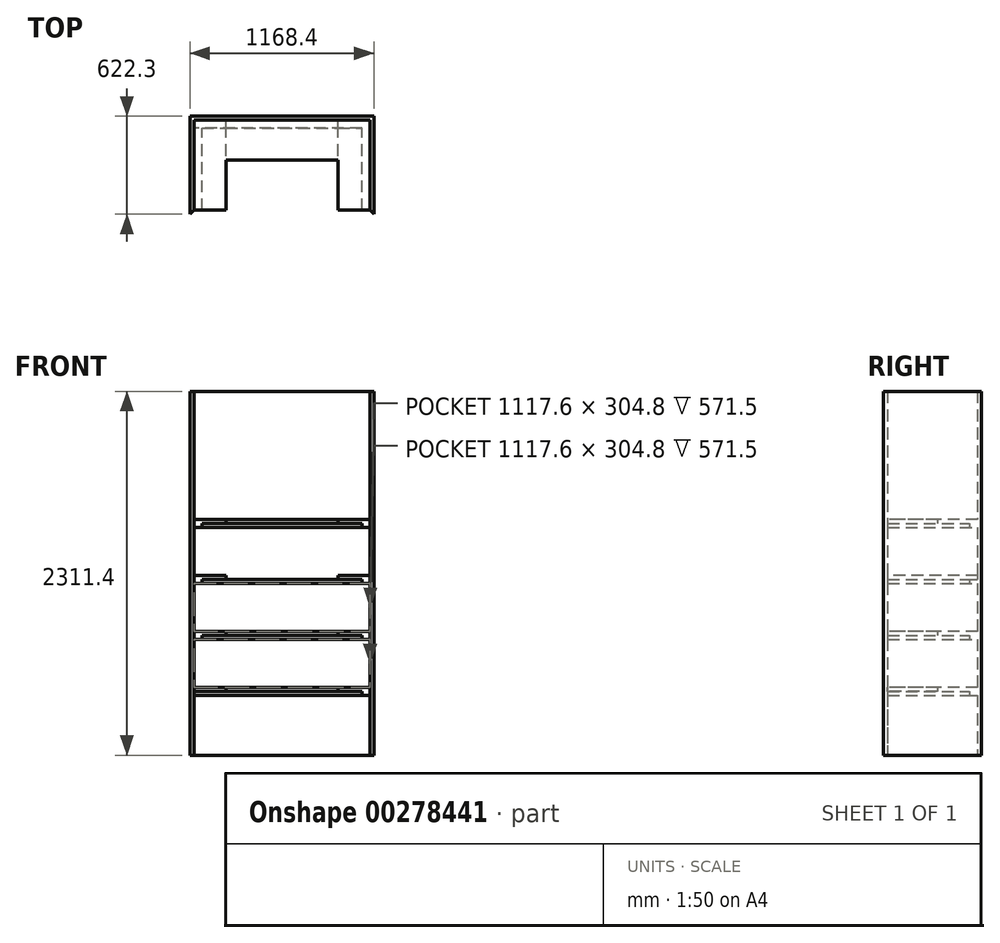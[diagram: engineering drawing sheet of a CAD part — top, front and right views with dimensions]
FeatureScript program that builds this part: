
annotation { "Feature Type Name" : "Feature", "Feature Type Description" : "" }
export const myFeature = defineFeature(function(context is Context, id is Id, definition is map)
    precondition{}
    {
        {
            var Q0;
            Q0=qCreatedBy(makeId("Top.planeOp"),FACE);
            var sketch = newSketch(context, id + "F0", { "sketchPlane" : qUnion([Q0])});
            skLineSegment(sketch, "E0.bottom", {"start": v(558.8, -285.75) * mm, "end": v(368.3, -285.75) * mm});
            skLineSegment(sketch, "E0.top", {"start": v(558.8, 285.75) * mm, "end": v(-558.8, 285.75) * mm});
            skLineSegment(sketch, "E0.left", {"start": v(558.8, -285.75) * mm, "end": v(558.8, 285.75) * mm});
            skLineSegment(sketch, "E0.right", {"start": v(-558.8, -285.75) * mm, "end": v(-558.8, 285.75) * mm});
            skPoint(sketch, "E0.middle", {"position": v(0, 0) * mm});
            skPoint(sketch, "E1", {"position": v(368.3, -285.75) * mm});
            skPoint(sketch, "E2", {"position": v(-368.3, -285.75) * mm});
            skLineSegment(sketch, "E3", {"start": v(-368.3, -285.75) * mm, "end": v(-558.8, -285.75) * mm});
            skLineSegment(sketch, "E4.0", {"start": v(584.2, -311.15) * mm, "end": v(368.3, -311.15) * mm});
            skLineSegment(sketch, "E4.1", {"start": v(-368.3, -311.15) * mm, "end": v(-584.2, -311.15) * mm});
            skLineSegment(sketch, "E4.2", {"start": v(-584.2, -311.15) * mm, "end": v(-584.2, 311.15) * mm});
            skLineSegment(sketch, "E4.3", {"start": v(584.2, 311.15) * mm, "end": v(-584.2, 311.15) * mm});
            skLineSegment(sketch, "E4.4", {"start": v(584.2, -311.15) * mm, "end": v(584.2, 311.15) * mm});
            skLineSegment(sketch, "E5", {"start": v(-368.3, -285.75) * mm, "end": v(-368.3, -311.15) * mm});
            skLineSegment(sketch, "E6", {"start": v(368.3, -285.75) * mm, "end": v(368.3, -311.15) * mm});
            skLineSegment(sketch, "E7", {"start": v(-558.8, -285.75) * mm, "end": v(-584.2, -311.15) * mm});
            skLineSegment(sketch, "E8", {"start": v(558.8, -285.75) * mm, "end": v(584.2, -311.15) * mm});
            skLineSegment(sketch, "E9", {"start": v(-584.2, 311.15) * mm, "end": v(-558.8, 285.75) * mm});
            skLineSegment(sketch, "E10", {"start": v(584.2, 311.15) * mm, "end": v(558.8, 285.75) * mm});
            skSolve(sketch);
        }
        {
            var Q0;
            Q0=makeQuery(id+"F0.imprint","IMPRINT",FACE,{"disambiguationData":[TD([[makeQuery(id+"F0.imprint","IMPRINT",EDGE,{"derivedFrom":sQuery(id+"F0.wireOp",EDGE,"E0.top")}),-1.0]])]});
            extrude(context, id + "F1", {"entities" : qUnion([Q0]), "depth" : 2311.4 * mm});
        }
        {
            var Q0;
            Q0=makeQuery(id+"F1.opExtrude","SWEPT_FACE",FACE,{"disambiguationData":[OSD([sQuery(id+"F0.wireOp",EDGE,"E0.top")])]});
            var sketch = newSketch(context, id + "F2", { "sketchPlane" : qUnion([Q0])});
            skLineSegment(sketch, "E11.0", {"start": v(-558.8, 2311.4) * mm, "end": v(-558.8, 0) * mm});
            skLineSegment(sketch, "E12.0", {"start": v(558.8, 0) * mm, "end": v(-558.8, 0) * mm});
            skLineSegment(sketch, "E13.0", {"start": v(558.8, 2311.4) * mm, "end": v(-558.8, 2311.4) * mm});
            skLineSegment(sketch, "E14.0", {"start": v(558.8, 2311.4) * mm, "end": v(558.8, 0) * mm});
            skLineSegment(sketch, "E15", {"start": v(-558.8, 406.4) * mm, "end": v(558.8, 406.4) * mm});
            skLineSegment(sketch, "E16", {"start": v(558.8, 381) * mm, "end": v(-558.8, 381) * mm});
            skLineSegment(sketch, "E17", {"start": v(-558.8, 736.6) * mm, "end": v(558.8, 736.6) * mm});
            skLineSegment(sketch, "E18", {"start": v(-558.8, 762) * mm, "end": v(558.8, 762) * mm});
            skLineSegment(sketch, "E19", {"start": v(-558.8, 1092.2) * mm, "end": v(558.8, 1092.2) * mm});
            skLineSegment(sketch, "E20", {"start": v(-558.8, 1117.6) * mm, "end": v(558.8, 1117.6) * mm});
            skLineSegment(sketch, "E21.top", {"start": v(-558.8, 431.8) * mm, "end": v(558.8, 431.8) * mm});
            skLineSegment(sketch, "E21.left", {"start": v(-558.8, 406.4) * mm, "end": v(-558.8, 431.8) * mm});
            skLineSegment(sketch, "E21.right", {"start": v(558.8, 406.4) * mm, "end": v(558.8, 431.8) * mm});
            skLineSegment(sketch, "E22.top", {"start": v(-558.8, 787.4) * mm, "end": v(558.8, 787.4) * mm});
            skLineSegment(sketch, "E22.left", {"start": v(-558.8, 762) * mm, "end": v(-558.8, 787.4) * mm});
            skLineSegment(sketch, "E22.right", {"start": v(558.8, 762) * mm, "end": v(558.8, 787.4) * mm});
            skLineSegment(sketch, "E23.top", {"start": v(-558.8, 1143) * mm, "end": v(558.8, 1143) * mm});
            skLineSegment(sketch, "E23.left", {"start": v(-558.8, 1117.6) * mm, "end": v(-558.8, 1143) * mm});
            skLineSegment(sketch, "E23.right", {"start": v(558.8, 1117.6) * mm, "end": v(558.8, 1143) * mm});
            skLineSegment(sketch, "E24.bottom", {"start": v(558.8, 1447.8) * mm, "end": v(-558.8, 1447.8) * mm});
            skLineSegment(sketch, "E24.top", {"start": v(558.8, 1473.2) * mm, "end": v(-558.8, 1473.2) * mm});
            skLineSegment(sketch, "E24.left", {"start": v(558.8, 1447.8) * mm, "end": v(558.8, 1473.2) * mm});
            skLineSegment(sketch, "E24.right", {"start": v(-558.8, 1447.8) * mm, "end": v(-558.8, 1473.2) * mm});
            skLineSegment(sketch, "E25", {"start": v(558.8, 1498.6) * mm, "end": v(-558.8, 1498.6) * mm});
            skSolve(sketch);
        }
        {
            var Q0;
            Q0=makeQuery(id+"F0.imprint","IMPRINT",FACE,{"disambiguationData":[TD([[makeQuery(id+"F0.imprint","IMPRINT",EDGE,{"derivedFrom":sQuery(id+"F0.wireOp",EDGE,"E0.right")}),1.0]])]});
            extrude(context, id + "F3", {"entities" : qUnion([Q0]), "operationType" : NewBodyOperationType.ADD, "depth" : 2311.4 * mm});
        }
        {
            var Q0;
            Q0=makeQuery(id+"F0.imprint","IMPRINT",FACE,{"disambiguationData":[TD([[makeQuery(id+"F0.imprint","IMPRINT",EDGE,{"derivedFrom":sQuery(id+"F0.wireOp",EDGE,"E0.left")}),-1.0]])]});
            extrude(context, id + "F4", {"entities" : qUnion([Q0]), "operationType" : NewBodyOperationType.ADD, "depth" : 2311.4 * mm});
        }
        {
            var Q0;
            Q0=makeQuery(id+"F3.opExtrude","SWEPT_FACE",FACE,{"disambiguationData":[OSD([sQuery(id+"F0.wireOp",EDGE,"E4.2")])]});
            var sketch = newSketch(context, id + "F5", { "sketchPlane" : qUnion([Q0])});
            skLineSegment(sketch, "E26.0", {"start": v(311.15, 2311.4) * mm, "end": v(311.15, 0) * mm});
            skLineSegment(sketch, "E27.0", {"start": v(-285.75, 2311.4) * mm, "end": v(-285.75, 0) * mm});
            skLineSegment(sketch, "E28.0", {"start": v(311.15, 0) * mm, "end": v(-311.15, 0) * mm});
            skPoint(sketch, "E29", {"position": v(311.15, 381) * mm});
            skPoint(sketch, "E30", {"position": v(311.15, 406.4) * mm});
            skPoint(sketch, "E31", {"position": v(311.15, 431.8) * mm});
            skPoint(sketch, "E32", {"position": v(311.15, 736.6) * mm});
            skPoint(sketch, "E33", {"position": v(311.15, 762) * mm});
            skPoint(sketch, "E34", {"position": v(311.15, 787.4) * mm});
            skPoint(sketch, "E35", {"position": v(311.15, 1092.2) * mm});
            skPoint(sketch, "E36", {"position": v(311.15, 1117.6) * mm});
            skPoint(sketch, "E37", {"position": v(311.15, 1143) * mm});
            skPoint(sketch, "E38", {"position": v(311.15, 0) * mm});
            skPoint(sketch, "E39", {"position": v(311.15, 2057.4) * mm});
            skLineSegment(sketch, "E40.left", {"start": v(311.15, 736.6) * mm, "end": v(311.15, 762) * mm});
            skLineSegment(sketch, "E40.right", {"start": v(-285.75, 736.6) * mm, "end": v(-285.75, 762) * mm});
            skLineSegment(sketch, "E41.left", {"start": v(311.15, 1092.2) * mm, "end": v(311.15, 1117.6) * mm});
            skLineSegment(sketch, "E41.right", {"start": v(-285.75, 1092.2) * mm, "end": v(-285.75, 1117.6) * mm});
            skPoint(sketch, "E42", {"position": v(311.15, 1447.8) * mm});
            skPoint(sketch, "E43", {"position": v(311.15, 1473.2) * mm});
            skPoint(sketch, "E44", {"position": v(311.15, 1498.6) * mm});
            skLineSegment(sketch, "E45.left", {"start": v(311.15, 1473.2) * mm, "end": v(311.15, 1498.6) * mm});
            skLineSegment(sketch, "E45.right", {"start": v(-285.75, 1473.2) * mm, "end": v(-285.75, 1498.6) * mm});
            skLineSegment(sketch, "E46.0", {"start": v(285.75, 2311.4) * mm, "end": v(285.75, 0) * mm});
            skPoint(sketch, "E47", {"position": v(285.75, 1498.6) * mm});
            skPoint(sketch, "E48", {"position": v(285.75, 1473.2) * mm});
            skPoint(sketch, "E49", {"position": v(285.75, 1447.8) * mm});
            skLineSegment(sketch, "E50", {"start": v(285.75, 1498.6) * mm, "end": v(-285.75, 1498.6) * mm});
            skLineSegment(sketch, "E51", {"start": v(285.75, 1473.2) * mm, "end": v(-285.75, 1473.2) * mm});
            skLineSegment(sketch, "E52", {"start": v(285.75, 1447.8) * mm, "end": v(-285.75, 1447.8) * mm});
            skLineSegment(sketch, "E53", {"start": v(285.75, 1092.2) * mm, "end": v(-285.75, 1092.2) * mm});
            skLineSegment(sketch, "E54", {"start": v(285.75, 1117.6) * mm, "end": v(-285.75, 1117.6) * mm});
            skLineSegment(sketch, "E55", {"start": v(285.75, 1143) * mm, "end": v(-285.75, 1143) * mm});
            skLineSegment(sketch, "E56", {"start": v(285.75, 787.4) * mm, "end": v(-285.75, 787.4) * mm});
            skLineSegment(sketch, "E57", {"start": v(285.75, 762) * mm, "end": v(-285.75, 762) * mm});
            skLineSegment(sketch, "E58", {"start": v(285.75, 736.6) * mm, "end": v(-285.75, 736.6) * mm});
            skLineSegment(sketch, "E59", {"start": v(285.75, 381) * mm, "end": v(-285.75, 381) * mm});
            skLineSegment(sketch, "E60", {"start": v(285.75, 406.4) * mm, "end": v(-285.75, 406.4) * mm});
            skLineSegment(sketch, "E61", {"start": v(285.75, 431.8) * mm, "end": v(-285.75, 431.8) * mm});
            skSolve(sketch);
        }
        {
            var Q0;
            Q0=makeQuery(id+"F3.opExtrude","SWEPT_FACE",FACE,{"disambiguationData":[OSD([sQuery(id+"F0.wireOp",EDGE,"E4.2")])]});
            var sketch = newSketch(context, id + "F6", { "sketchPlane" : qUnion([Q0])});
            skLineSegment(sketch, "E62.0", {"start": v(311.15, 2311.4) * mm, "end": v(311.15, 0) * mm});
            skLineSegment(sketch, "E63.0", {"start": v(311.15, 0) * mm, "end": v(-311.15, 0) * mm});
            skLineSegment(sketch, "E64.0", {"start": v(-285.75, 2311.4) * mm, "end": v(-285.75, 0) * mm});
            skPoint(sketch, "E65", {"position": v(311.15, 381) * mm});
            skPoint(sketch, "E66", {"position": v(-285.75, 381) * mm});
            skPoint(sketch, "E67", {"position": v(311.15, 406.4) * mm});
            skPoint(sketch, "E68", {"position": v(311.15, 431.8) * mm});
            skLineSegment(sketch, "E69", {"start": v(311.15, 381) * mm, "end": v(-285.75, 381) * mm});
            skLineSegment(sketch, "E70", {"start": v(311.15, 406.4) * mm, "end": v(-285.75, 406.4) * mm});
            skLineSegment(sketch, "E71", {"start": v(311.15, 431.8) * mm, "end": v(-285.75, 431.8) * mm});
            skSolve(sketch);
        }
        {
            var Q0;
            Q0=makeQuery(id+"F3.opExtrude","SWEPT_FACE",FACE,{"disambiguationData":[OSD([sQuery(id+"F0.wireOp",EDGE,"E0.right")])]});
            var sketch = newSketch(context, id + "F7", { "sketchPlane" : qUnion([Q0])});
            skLineSegment(sketch, "E72.0", {"start": v(-285.75, 2311.4) * mm, "end": v(-285.75, 0) * mm});
            skLineSegment(sketch, "E73.0", {"start": v(285.75, 2311.4) * mm, "end": v(285.75, 0) * mm});
            skLineSegment(sketch, "E74.0", {"start": v(-311.15, 381) * mm, "end": v(285.75, 381) * mm});
            skLineSegment(sketch, "E75.0", {"start": v(-311.15, 406.4) * mm, "end": v(285.75, 406.4) * mm});
            skLineSegment(sketch, "E76.0", {"start": v(-311.15, 431.8) * mm, "end": v(285.75, 431.8) * mm});
            skLineSegment(sketch, "E77.0", {"start": v(-285.75, 736.6) * mm, "end": v(285.75, 736.6) * mm});
            skLineSegment(sketch, "E78.0", {"start": v(-285.75, 762) * mm, "end": v(285.75, 762) * mm});
            skLineSegment(sketch, "E79.0", {"start": v(-285.75, 787.4) * mm, "end": v(285.75, 787.4) * mm});
            skLineSegment(sketch, "E80.0", {"start": v(-285.75, 1092.2) * mm, "end": v(285.75, 1092.2) * mm});
            skLineSegment(sketch, "E81.0", {"start": v(-285.75, 1117.6) * mm, "end": v(285.75, 1117.6) * mm});
            skLineSegment(sketch, "E82.0", {"start": v(-285.75, 1143) * mm, "end": v(285.75, 1143) * mm});
            skLineSegment(sketch, "E83.0", {"start": v(-285.75, 1447.8) * mm, "end": v(285.75, 1447.8) * mm});
            skLineSegment(sketch, "E84.0", {"start": v(-285.75, 1473.2) * mm, "end": v(285.75, 1473.2) * mm});
            skLineSegment(sketch, "E85.0", {"start": v(-285.75, 1498.6) * mm, "end": v(285.75, 1498.6) * mm});
            skLineSegment(sketch, "E86.0", {"start": v(-285.75, 2311.4) * mm, "end": v(285.75, 2311.4) * mm});
            skLineSegment(sketch, "E87", {"start": v(-285.75, 431.8) * mm, "end": v(285.75, 431.8) * mm});
            skLineSegment(sketch, "E88", {"start": v(-285.75, 406.4) * mm, "end": v(285.75, 406.4) * mm});
            skLineSegment(sketch, "E89", {"start": v(-285.75, 381) * mm, "end": v(285.75, 381) * mm});
            skSolve(sketch);
        }
        {
            var Q0;
            Q0=makeQuery(id+"F4.opExtrude","SWEPT_FACE",FACE,{"disambiguationData":[OSD([sQuery(id+"F0.wireOp",EDGE,"E0.left")])]});
            var sketch = newSketch(context, id + "F8", { "sketchPlane" : qUnion([Q0])});
            skLineSegment(sketch, "E90.0.0", {"start": v(311.15, 0) * mm, "end": v(311.15, 381) * mm});
            skLineSegment(sketch, "E90.0.1", {"start": v(311.15, 381) * mm, "end": v(-285.75, 381) * mm});
            skLineSegment(sketch, "E90.0.2", {"start": v(-285.75, 381) * mm, "end": v(-285.75, 0) * mm});
            skLineSegment(sketch, "E90.0.3", {"start": v(-285.75, 0) * mm, "end": v(311.15, 0) * mm});
            skLineSegment(sketch, "E91.0", {"start": v(285.75, 2311.4) * mm, "end": v(285.75, 0) * mm});
            skLineSegment(sketch, "E92.0.0", {"start": v(311.15, 381) * mm, "end": v(311.15, 406.4) * mm});
            skLineSegment(sketch, "E92.0.1", {"start": v(311.15, 406.4) * mm, "end": v(-285.75, 406.4) * mm});
            skLineSegment(sketch, "E92.0.2", {"start": v(-285.75, 406.4) * mm, "end": v(-285.75, 381) * mm});
            skLineSegment(sketch, "E92.0.3", {"start": v(-285.75, 381) * mm, "end": v(311.15, 381) * mm});
            skLineSegment(sketch, "E93.0.0", {"start": v(311.15, 406.4) * mm, "end": v(311.15, 431.8) * mm});
            skLineSegment(sketch, "E93.0.1", {"start": v(311.15, 431.8) * mm, "end": v(-285.75, 431.8) * mm});
            skLineSegment(sketch, "E93.0.2", {"start": v(-285.75, 431.8) * mm, "end": v(-285.75, 406.4) * mm});
            skLineSegment(sketch, "E93.0.3", {"start": v(-285.75, 406.4) * mm, "end": v(311.15, 406.4) * mm});
            skLineSegment(sketch, "E94.0.0", {"start": v(-285.75, 431.8) * mm, "end": v(311.15, 431.8) * mm});
            skLineSegment(sketch, "E94.0.1", {"start": v(311.15, 431.8) * mm, "end": v(311.15, 2311.4) * mm});
            skLineSegment(sketch, "E94.0.2", {"start": v(311.15, 2311.4) * mm, "end": v(-285.75, 2311.4) * mm});
            skLineSegment(sketch, "E94.0.3", {"start": v(-285.75, 2311.4) * mm, "end": v(-285.75, 431.8) * mm});
            skLineSegment(sketch, "E95.0", {"start": v(285.75, 736.6) * mm, "end": v(-285.75, 736.6) * mm});
            skLineSegment(sketch, "E96.0", {"start": v(285.75, 762) * mm, "end": v(-285.75, 762) * mm});
            skLineSegment(sketch, "E97.0", {"start": v(285.75, 787.4) * mm, "end": v(-285.75, 787.4) * mm});
            skLineSegment(sketch, "E98.0", {"start": v(285.75, 1092.2) * mm, "end": v(-285.75, 1092.2) * mm});
            skLineSegment(sketch, "E99.0", {"start": v(285.75, 1473.2) * mm, "end": v(-285.75, 1473.2) * mm});
            skLineSegment(sketch, "E100.0", {"start": v(285.75, 1447.8) * mm, "end": v(-285.75, 1447.8) * mm});
            skLineSegment(sketch, "E101.0", {"start": v(285.75, 1498.6) * mm, "end": v(-285.75, 1498.6) * mm});
            skLineSegment(sketch, "E102.0.0", {"start": v(285.75, 1498.6) * mm, "end": v(285.75, 2311.4) * mm});
            skLineSegment(sketch, "E102.0.1", {"start": v(285.75, 2311.4) * mm, "end": v(-285.75, 2311.4) * mm});
            skLineSegment(sketch, "E102.0.2", {"start": v(-285.75, 2311.4) * mm, "end": v(-285.75, 1498.6) * mm});
            skLineSegment(sketch, "E102.0.3", {"start": v(-285.75, 1498.6) * mm, "end": v(285.75, 1498.6) * mm});
            skLineSegment(sketch, "E103.0", {"start": v(285.75, 1117.6) * mm, "end": v(-285.75, 1117.6) * mm});
            skLineSegment(sketch, "E104.0", {"start": v(285.75, 1143) * mm, "end": v(-285.75, 1143) * mm});
            skSolve(sketch);
        }
        {
            var Q0;
            {var subQ0=sQuery(id+"F2.wireOp",EDGE,"E16");Q0=makeQuery(id+"F2.imprint","IMPRINT",FACE,{"disambiguationData":[TD([[makeQuery(id+"F2.imprint","IMPRINT",EDGE,{"derivedFrom":subQ0}),-1.0]])]});}
            var Q1;
            {var subQ0=sQuery(id+"F2.wireOp",EDGE,"E17");Q1=makeQuery(id+"F2.imprint","IMPRINT",FACE,{"disambiguationData":[TD([[makeQuery(id+"F2.imprint","IMPRINT",EDGE,{"derivedFrom":subQ0}),1.0]])]});}
            var Q2;
            {var subQ0=sQuery(id+"F2.wireOp",EDGE,"E19");Q2=makeQuery(id+"F2.imprint","IMPRINT",FACE,{"disambiguationData":[TD([[makeQuery(id+"F2.imprint","IMPRINT",EDGE,{"derivedFrom":subQ0}),1.0]])]});}
            var Q3;
            Q3=makeQuery(id+"F2.imprint","IMPRINT",FACE,{"disambiguationData":[TD([[makeQuery(id+"F2.imprint","IMPRINT",EDGE,{"derivedFrom":sQuery(id+"F2.wireOp",EDGE,"E24.bottom")}),-1.0]])]});
            extrude(context, id + "F9", {"entities" : qUnion([Q0, Q1, Q2, Q3]), "operationType" : NewBodyOperationType.ADD, "depth" : 50.8 * mm});
        }
        {
            var Q0;
            {var subQ0=sQuery(id+"F7.wireOp",EDGE,"E83.0");Q0=makeQuery(id+"F7.imprint","IMPRINT",FACE,{"disambiguationData":[TD([[makeQuery(id+"F7.imprint","IMPRINT",EDGE,{"derivedFrom":subQ0}),1.0]])]});}
            var Q1;
            {var subQ0=sQuery(id+"F7.wireOp",EDGE,"E80.0");Q1=makeQuery(id+"F7.imprint","IMPRINT",FACE,{"disambiguationData":[TD([[makeQuery(id+"F7.imprint","IMPRINT",EDGE,{"derivedFrom":subQ0}),1.0]])]});}
            var Q2;
            {var subQ0=sQuery(id+"F7.wireOp",EDGE,"E77.0");Q2=makeQuery(id+"F7.imprint","IMPRINT",FACE,{"disambiguationData":[TD([[makeQuery(id+"F7.imprint","IMPRINT",EDGE,{"derivedFrom":subQ0}),1.0]])]});}
            var Q3;
            {var subQ2=sQuery(id+"F7.wireOp",EDGE,"E88");Q3=makeQuery(id+"F7.imprint","IMPRINT",FACE,{"disambiguationData":[TD([[makeQuery(id+"F7.imprint","IMPRINT",EDGE,{"derivedFrom":subQ2}),-1.0]])]});}
            extrude(context, id + "F10", {"entities" : qUnion([Q0, Q1, Q2, Q3]), "operationType" : NewBodyOperationType.ADD, "depth" : 50.8 * mm});
        }
        {
            var Q0;
            {var subQ5=sQuery(id+"F8.wireOp",EDGE,"E92.0.2");Q0=makeQuery(id+"F8.imprint","IMPRINT",FACE,{"disambiguationData":[TD([[makeQuery(id+"F8.imprint","IMPRINT",EDGE,{"derivedFrom":subQ5}),1.0]])]});}
            var Q1;
            {var subQ0=sQuery(id+"F8.wireOp",EDGE,"E95.0");Q1=makeQuery(id+"F8.imprint","IMPRINT",FACE,{"disambiguationData":[TD([[makeQuery(id+"F8.imprint","IMPRINT",EDGE,{"derivedFrom":subQ0}),-1.0]])]});}
            var Q2;
            {var subQ0=sQuery(id+"F8.wireOp",EDGE,"E98.0");Q2=makeQuery(id+"F8.imprint","IMPRINT",FACE,{"disambiguationData":[TD([[makeQuery(id+"F8.imprint","IMPRINT",EDGE,{"derivedFrom":subQ0}),-1.0]])]});}
            var Q3;
            {var subQ0=sQuery(id+"F8.wireOp",EDGE,"E100.0");Q3=makeQuery(id+"F8.imprint","IMPRINT",FACE,{"disambiguationData":[TD([[makeQuery(id+"F8.imprint","IMPRINT",EDGE,{"derivedFrom":subQ0}),-1.0]])]});}
            extrude(context, id + "F11", {"entities" : qUnion([Q0, Q1, Q2, Q3]), "operationType" : NewBodyOperationType.ADD, "depth" : 50.8 * mm});
        }
        {
            var Q0;
            Q0=makeQuery(id+"F10.boolean.opBoolean","SPLIT",FACE,{"disambiguationData":[TD([makeQuery(id+"F9.opExtrude","SWEPT_FACE",FACE,{"disambiguationData":[OSD([sQuery(id+"F2.wireOp",EDGE,"E20")])]})])],"derivedFrom":makeQuery(id+"F3.opExtrude","SWEPT_FACE",FACE,{"disambiguationData":[OSD([sQuery(id+"F0.wireOp",EDGE,"E0.right")])]})});
            var sketch = newSketch(context, id + "F12", { "sketchPlane" : qUnion([Q0])});
            skLineSegment(sketch, "E105.0", {"start": v(-285.75, 431.8) * mm, "end": v(285.75, 431.8) * mm});
            skLineSegment(sketch, "E106.0", {"start": v(-285.75, 787.4) * mm, "end": v(285.75, 787.4) * mm});
            skLineSegment(sketch, "E107.0", {"start": v(-285.75, 1143) * mm, "end": v(285.75, 1143) * mm});
            skLineSegment(sketch, "E108.0", {"start": v(-285.75, 1498.6) * mm, "end": v(285.75, 1498.6) * mm});
            skLineSegment(sketch, "E109.0", {"start": v(-285.75, 736.6) * mm, "end": v(-285.75, 406.4) * mm});
            skLineSegment(sketch, "E110.0", {"start": v(285.75, 2311.4) * mm, "end": v(285.75, 0) * mm});
            skLineSegment(sketch, "E111.0", {"start": v(-285.75, 406.4) * mm, "end": v(285.75, 406.4) * mm});
            skLineSegment(sketch, "E112.0.0", {"start": v(-311.15, 0) * mm, "end": v(-285.75, 0) * mm});
            skLineSegment(sketch, "E112.0.1", {"start": v(-285.75, 0) * mm, "end": v(-285.75, 381) * mm});
            skLineSegment(sketch, "E112.0.2", {"start": v(-285.75, 381) * mm, "end": v(-285.75, 406.4) * mm});
            skLineSegment(sketch, "E112.0.3", {"start": v(-285.75, 406.4) * mm, "end": v(-285.75, 736.6) * mm});
            skLineSegment(sketch, "E112.0.4", {"start": v(-285.75, 736.6) * mm, "end": v(-285.75, 762) * mm});
            skLineSegment(sketch, "E112.0.5", {"start": v(-285.75, 762) * mm, "end": v(-285.75, 1092.2) * mm});
            skLineSegment(sketch, "E112.0.6", {"start": v(-285.75, 1092.2) * mm, "end": v(-285.75, 1117.6) * mm});
            skLineSegment(sketch, "E112.0.7", {"start": v(-285.75, 1117.6) * mm, "end": v(-285.75, 1447.8) * mm});
            skLineSegment(sketch, "E112.0.8", {"start": v(-285.75, 1447.8) * mm, "end": v(-285.75, 1473.2) * mm});
            skLineSegment(sketch, "E112.0.9", {"start": v(-285.75, 1473.2) * mm, "end": v(-285.75, 2311.4) * mm});
            skLineSegment(sketch, "E112.0.10", {"start": v(-285.75, 2311.4) * mm, "end": v(-311.15, 2311.4) * mm});
            skLineSegment(sketch, "E112.0.11", {"start": v(-311.15, 2311.4) * mm, "end": v(-311.15, 0) * mm});
            skLineSegment(sketch, "E113.0", {"start": v(-285.75, 762) * mm, "end": v(285.75, 762) * mm});
            skLineSegment(sketch, "E114.0.0", {"start": v(-285.75, 1117.6) * mm, "end": v(285.75, 1117.6) * mm});
            skLineSegment(sketch, "E114.0.2", {"start": v(285.75, 1117.6) * mm, "end": v(-285.75, 1117.6) * mm});
            skLineSegment(sketch, "E114.0.4", {"start": v(-285.75, 1117.6) * mm, "end": v(234.95, 1117.6) * mm});
            skLineSegment(sketch, "E114.0.6", {"start": v(234.95, 1117.6) * mm, "end": v(-285.75, 1117.6) * mm});
            skLineSegment(sketch, "E115.0", {"start": v(-285.75, 1473.2) * mm, "end": v(285.75, 1473.2) * mm});
            skSolve(sketch);
        }
        {
            var Q0;
            {var subQ0=sQuery(id+"F12.wireOp",EDGE,"E105.0");Q0=makeQuery(id+"F12.imprint","IMPRINT",FACE,{"disambiguationData":[TD([[makeQuery(id+"F12.imprint","IMPRINT",EDGE,{"derivedFrom":subQ0}),-1.0]])]});}
            var Q1;
            {var subQ0=sQuery(id+"F12.wireOp",EDGE,"E106.0");Q1=makeQuery(id+"F12.imprint","IMPRINT",FACE,{"disambiguationData":[TD([[makeQuery(id+"F12.imprint","IMPRINT",EDGE,{"derivedFrom":subQ0}),-1.0]])]});}
            var Q2;
            {var subQ3=sQuery(id+"F12.wireOp",EDGE,"E107.0");Q2=makeQuery(id+"F12.imprint","IMPRINT",FACE,{"disambiguationData":[TD([[makeQuery(id+"F12.imprint","IMPRINT",EDGE,{"derivedFrom":subQ3}),-1.0]])]});}
            var Q3;
            {var subQ0=sQuery(id+"F12.wireOp",EDGE,"E108.0");Q3=makeQuery(id+"F12.imprint","IMPRINT",FACE,{"disambiguationData":[TD([[makeQuery(id+"F12.imprint","IMPRINT",EDGE,{"derivedFrom":subQ0}),-1.0]])]});}
            extrude(context, id + "F13", {"entities" : qUnion([Q0, Q1, Q2, Q3]), "operationType" : NewBodyOperationType.ADD, "depth" : 203.2 * mm});
        }
        {
            var Q0;
            Q0=makeQuery(id+"F11.boolean.opBoolean","SPLIT",FACE,{"disambiguationData":[TD([makeQuery(id+"F9.opExtrude","SWEPT_FACE",FACE,{"disambiguationData":[OSD([sQuery(id+"F2.wireOp",EDGE,"E19")])]})])],"derivedFrom":makeQuery(id+"F4.opExtrude","SWEPT_FACE",FACE,{"disambiguationData":[OSD([sQuery(id+"F0.wireOp",EDGE,"E0.left")])]})});
            var sketch = newSketch(context, id + "F14", { "sketchPlane" : qUnion([Q0])});
            skLineSegment(sketch, "E116.0.0", {"start": v(-285.75, 406.4) * mm, "end": v(285.75, 406.4) * mm});
            skLineSegment(sketch, "E116.0.1", {"start": v(285.75, 406.4) * mm, "end": v(285.75, 736.6) * mm});
            skLineSegment(sketch, "E116.0.2", {"start": v(285.75, 736.6) * mm, "end": v(-285.75, 736.6) * mm});
            skLineSegment(sketch, "E116.0.3", {"start": v(-285.75, 736.6) * mm, "end": v(-285.75, 406.4) * mm});
            skLineSegment(sketch, "E117.0", {"start": v(285.75, 1092.2) * mm, "end": v(285.75, 762) * mm});
            skPoint(sketch, "E118.0", {"position": v(-285.75, 787.4) * mm});
            skLineSegment(sketch, "E119.0", {"start": v(285.75, 762) * mm, "end": v(-285.75, 762) * mm});
            skLineSegment(sketch, "E120.0", {"start": v(285.75, 1447.8) * mm, "end": v(285.75, 1117.6) * mm});
            skLineSegment(sketch, "E121.0", {"start": v(285.75, 1117.6) * mm, "end": v(-285.75, 1117.6) * mm});
            skPoint(sketch, "E122.0", {"position": v(-285.75, 1143) * mm});
            skLineSegment(sketch, "E123.0", {"start": v(285.75, 2311.4) * mm, "end": v(285.75, 1473.2) * mm});
            skLineSegment(sketch, "E124.0", {"start": v(285.75, 1473.2) * mm, "end": v(-285.75, 1473.2) * mm});
            skPoint(sketch, "E125.0", {"position": v(-285.75, 1498.6) * mm});
            skLineSegment(sketch, "E126", {"start": v(-285.75, 1498.6) * mm, "end": v(285.75, 1498.6) * mm});
            skLineSegment(sketch, "E127.0", {"start": v(-285.75, 2311.4) * mm, "end": v(-285.75, 0) * mm});
            skLineSegment(sketch, "E128", {"start": v(-285.75, 1143) * mm, "end": v(285.75, 1143) * mm});
            skLineSegment(sketch, "E129", {"start": v(-285.75, 1143) * mm, "end": v(-285.75, 1117.6) * mm});
            skLineSegment(sketch, "E130", {"start": v(-285.75, 787.4) * mm, "end": v(285.75, 787.4) * mm});
            skPoint(sketch, "E131.0", {"position": v(-285.75, 431.8) * mm});
            skLineSegment(sketch, "E132", {"start": v(-285.75, 431.8) * mm, "end": v(285.75, 431.8) * mm});
            skSolve(sketch);
        }
        {
            var Q0;
            {var subQ0=sQuery(id+"F14.wireOp",EDGE,"E124.0");Q0=makeQuery(id+"F14.imprint","IMPRINT",FACE,{"disambiguationData":[TD([[makeQuery(id+"F14.imprint","IMPRINT",EDGE,{"derivedFrom":subQ0}),-1.0]])]});}
            var Q1;
            {var subQ0=sQuery(id+"F14.wireOp",EDGE,"E119.0");Q1=makeQuery(id+"F14.imprint","IMPRINT",FACE,{"disambiguationData":[TD([[makeQuery(id+"F14.imprint","IMPRINT",EDGE,{"derivedFrom":subQ0}),-1.0]])]});}
            var Q2;
            {var subQ0=sQuery(id+"F14.wireOp",EDGE,"E116.0.0");Q2=makeQuery(id+"F14.imprint","IMPRINT",FACE,{"disambiguationData":[TD([[makeQuery(id+"F14.imprint","IMPRINT",EDGE,{"derivedFrom":subQ0}),1.0]])]});}
            var Q3;
            {var subQ0=sQuery(id+"F14.wireOp",EDGE,"E121.0");Q3=makeQuery(id+"F14.imprint","IMPRINT",FACE,{"disambiguationData":[TD([[makeQuery(id+"F14.imprint","IMPRINT",EDGE,{"derivedFrom":subQ0}),-1.0]])]});}
            extrude(context, id + "F15", {"entities" : qUnion([Q0, Q1, Q2, Q3]), "operationType" : NewBodyOperationType.ADD, "depth" : 203.2 * mm});
        }
        {
            var Q0;
            Q0=makeQuery(id+"F2.imprint","IMPRINT",FACE,{"disambiguationData":[TD([[makeQuery(id+"F2.imprint","IMPRINT",EDGE,{"derivedFrom":sQuery(id+"F2.wireOp",EDGE,"E20")}),1.0]])]});
            var sketch = newSketch(context, id + "F16", { "sketchPlane" : qUnion([Q0])});
            skLineSegment(sketch, "E133.0.0", {"start": v(558.8, 431.8) * mm, "end": v(-558.8, 431.8) * mm});
            skLineSegment(sketch, "E133.0.1", {"start": v(-558.8, 431.8) * mm, "end": v(-558.8, 406.4) * mm});
            skLineSegment(sketch, "E133.0.2", {"start": v(-558.8, 406.4) * mm, "end": v(558.8, 406.4) * mm});
            skLineSegment(sketch, "E133.0.3", {"start": v(558.8, 406.4) * mm, "end": v(558.8, 431.8) * mm});
            skLineSegment(sketch, "E134.0", {"start": v(-355.6, 431.8) * mm, "end": v(-355.6, 406.4) * mm});
            skLineSegment(sketch, "E135.0", {"start": v(355.6, 431.8) * mm, "end": v(355.6, 406.4) * mm});
            skLineSegment(sketch, "E136.0.0", {"start": v(558.8, 787.4) * mm, "end": v(355.6, 787.4) * mm});
            skLineSegment(sketch, "E136.0.1", {"start": v(-558.8, 787.4) * mm, "end": v(-558.8, 762) * mm});
            skLineSegment(sketch, "E136.0.2", {"start": v(-558.8, 762) * mm, "end": v(355.6, 762) * mm});
            skLineSegment(sketch, "E136.0.3", {"start": v(558.8, 762) * mm, "end": v(558.8, 787.4) * mm});
            skLineSegment(sketch, "E137.0", {"start": v(355.6, 787.4) * mm, "end": v(355.6, 762) * mm});
            skLineSegment(sketch, "E138.0", {"start": v(-355.6, 787.4) * mm, "end": v(-355.6, 762) * mm});
            skLineSegment(sketch, "E139.0", {"start": v(-558.8, 1143) * mm, "end": v(355.6, 1143) * mm});
            skLineSegment(sketch, "E140.0", {"start": v(-558.8, 1117.6) * mm, "end": v(558.8, 1117.6) * mm});
            skLineSegment(sketch, "E141.0", {"start": v(-355.6, 1143) * mm, "end": v(-355.6, 1143) * mm});
            skLineSegment(sketch, "E142.0.0", {"start": v(-355.6, 1117.6) * mm, "end": v(355.6, 1117.6) * mm});
            skLineSegment(sketch, "E142.0.2", {"start": v(355.6, 1117.6) * mm, "end": v(-355.6, 1117.6) * mm});
            skLineSegment(sketch, "E143.0.0", {"start": v(508, 1092.2) * mm, "end": v(508, 1117.6) * mm});
            skLineSegment(sketch, "E143.0.1", {"start": v(508, 1117.6) * mm, "end": v(355.6, 1117.6) * mm});
            skLineSegment(sketch, "E143.0.3", {"start": v(-355.6, 1117.6) * mm, "end": v(-508, 1117.6) * mm});
            skLineSegment(sketch, "E143.0.4", {"start": v(-508, 1117.6) * mm, "end": v(-508, 1092.2) * mm});
            skLineSegment(sketch, "E143.0.5", {"start": v(-508, 1092.2) * mm, "end": v(508, 1092.2) * mm});
            skLineSegment(sketch, "E144.0", {"start": v(355.6, 1143) * mm, "end": v(355.6, 1117.6) * mm});
            skLineSegment(sketch, "E145.0.0", {"start": v(558.8, 1473.2) * mm, "end": v(558.8, 1498.6) * mm});
            skLineSegment(sketch, "E145.0.1", {"start": v(558.8, 1498.6) * mm, "end": v(355.6, 1498.6) * mm});
            skLineSegment(sketch, "E145.0.2", {"start": v(-558.8, 1498.6) * mm, "end": v(-558.8, 1473.2) * mm});
            skLineSegment(sketch, "E145.0.3", {"start": v(-558.8, 1473.2) * mm, "end": v(-355.6, 1473.2) * mm});
            skLineSegment(sketch, "E146.0", {"start": v(-355.6, 1498.6) * mm, "end": v(-355.6, 1473.2) * mm});
            skLineSegment(sketch, "E147.0", {"start": v(355.6, 1498.6) * mm, "end": v(355.6, 1473.2) * mm});
            skLineSegment(sketch, "E148", {"start": v(-355.6, 1498.6) * mm, "end": v(-558.8, 1498.6) * mm});
            skLineSegment(sketch, "E149", {"start": v(-355.6, 1473.2) * mm, "end": v(355.6, 1473.2) * mm});
            skLineSegment(sketch, "E150", {"start": v(355.6, 1473.2) * mm, "end": v(558.8, 1473.2) * mm});
            skLineSegment(sketch, "E151", {"start": v(355.6, 1498.6) * mm, "end": v(-355.6, 1498.6) * mm});
            skLineSegment(sketch, "E152", {"start": v(-355.6, 1143) * mm, "end": v(-355.6, 1117.6) * mm});
            skLineSegment(sketch, "E153", {"start": v(-355.6, 1117.6) * mm, "end": v(-355.6, 1117.6) * mm});
            skLineSegment(sketch, "E154", {"start": v(355.6, 1117.6) * mm, "end": v(355.6, 1117.6) * mm});
            skLineSegment(sketch, "E155", {"start": v(355.6, 1143) * mm, "end": v(558.8, 1143) * mm});
            skLineSegment(sketch, "E156", {"start": v(-355.6, 787.4) * mm, "end": v(-558.8, 787.4) * mm});
            skLineSegment(sketch, "E157", {"start": v(-355.6, 762) * mm, "end": v(-355.6, 762) * mm});
            skLineSegment(sketch, "E158", {"start": v(355.6, 787.4) * mm, "end": v(-355.6, 787.4) * mm});
            skLineSegment(sketch, "E159", {"start": v(355.6, 762) * mm, "end": v(558.8, 762) * mm});
            skSolve(sketch);
        }
        {
            var Q0;
            {var subQ0=sQuery(id+"F16.wireOp",EDGE,"E134.0");Q0=makeQuery(id+"F16.imprint","IMPRINT",FACE,{"disambiguationData":[TD([[makeQuery(id+"F16.imprint","IMPRINT",EDGE,{"derivedFrom":subQ0}),1.0]])]});}
            var Q1;
            Q1=makeQuery(id+"F16.imprint","IMPRINT",FACE,{"disambiguationData":[TD([[makeQuery(id+"F16.imprint","IMPRINT",EDGE,{"derivedFrom":sQuery(id+"F16.wireOp",EDGE,"E146.0")}),1.0]])]});
            var Q2;
            {var subQ0=sQuery(id+"F16.wireOp",EDGE,"E137.0");Q2=makeQuery(id+"F16.imprint","IMPRINT",FACE,{"disambiguationData":[TD([[makeQuery(id+"F16.imprint","IMPRINT",EDGE,{"derivedFrom":subQ0}),-1.0]])]});}
            var Q3;
            Q3=makeQuery(id+"F16.imprint","IMPRINT",FACE,{"disambiguationData":[TD([[makeQuery(id+"F16.imprint","IMPRINT",EDGE,{"derivedFrom":sQuery(id+"F16.wireOp",EDGE,"E142.0.2")}),1.0]])]});
            extrude(context, id + "F17", {"entities" : qUnion([Q0, Q1, Q2, Q3]), "operationType" : NewBodyOperationType.ADD, "depth" : 254 * mm});
        }
    });
